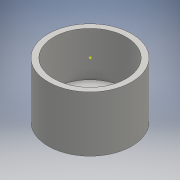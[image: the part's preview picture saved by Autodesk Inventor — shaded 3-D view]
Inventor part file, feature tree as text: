
AUTODESK INVENTOR PART (.ipt)
format: ipt  version: 2016 (Build 200138000, 138)  size: 93,696 bytes
history: native  units: mm
features: extrude x1, other x1, hole x1, sketch x1
ambient origin geometry x8: Origin, YZ Plane, XZ Plane, XY Plane, X Axis, Y Axis, Z Axis, Center Point
bodies: Solid1 (feature_tree)
feature tree (4):
  extrude  "Extrusion1"  Depth=5.0mm TaperAngle=0.0deg
  other  "Work Point1"
  hole  "Hole1"  [1 undecoded]
  sketch  "Sketch1"  dims[d0=7.5mm d1=5.0mm d2=0.0mm d3=10.0mm d4=10.0mm d5=6.5mm d6=6.0mm d7=4.0mm d8=2.0mm d9=90.0deg d10=4.0mm d11=0.0mm]
note: 1 required parameter value undecoded (feature->parameter linkage not recoverable at this tier; creation-order binding heuristic only, values carry confidence <= 0.55)
